annotation { "Feature Type Name" : "Feature", "Feature Type Description" : "" }
export const myFeature = defineFeature(function(context is Context, id is Id, definition is map)
    precondition{}
    {
        {
            var Q0;
            Q0=qCreatedBy(makeId("Top.planeOp"),FACE);
            var sketch = newSketch(context, id + "F0", { "sketchPlane" : qUnion([Q0])});
            skLineSegment(sketch, "E0.bottom", {"start": v(-20, 20) * mm, "end": v(20, 20) * mm});
            skLineSegment(sketch, "E0.top", {"start": v(-20, -20) * mm, "end": v(20, -20) * mm});
            skLineSegment(sketch, "E0.left", {"start": v(-20, 20) * mm, "end": v(-20, -20) * mm});
            skLineSegment(sketch, "E0.right", {"start": v(20, 20) * mm, "end": v(20, -20) * mm});
            skLineSegment(sketch, "E1", {"start": v(-20, 0) * mm, "end": v(20, 0) * mm, "construction": true});
            skSolve(sketch);
        }
        {
            var Q0;
            Q0=makeQuery(id+"F0.imprint","IMPRINT",FACE,{"disambiguationData":[TD([[makeQuery(id+"F0.imprint","IMPRINT",EDGE,{"derivedFrom":sQuery(id+"F0.wireOp",EDGE,"E0.bottom")}),-1.0]])]});
            extrude(context, id + "F1", {"entities" : qUnion([Q0]), "oppositeDirection" : true, "depth" : 40 * mm, "offsetDistance" : 25.4 * mm});
        }
        {
            var Q0;
            Q0=makeQuery(id+"F1.opExtrude","CAP_FACE",FACE,{"disambiguationData":[OSD([sQuery(id+"F0.wireOp",EDGE,"E0.bottom"),sQuery(id+"F0.wireOp",EDGE,"E0.top"),sQuery(id+"F0.wireOp",EDGE,"E0.left"),sQuery(id+"F0.wireOp",EDGE,"E0.right")])],"isStart":true});
            var sketch = newSketch(context, id + "F2", { "sketchPlane" : qUnion([Q0])});
            skLineSegment(sketch, "E2", {"start": v(-3.88, 5.43) * mm, "end": v(-3.88, -20) * mm});
            skLineSegment(sketch, "E3", {"start": v(4.12, 5.43) * mm, "end": v(4.12, -20) * mm});
            skLineSegment(sketch, "E4", {"start": v(4.12, -20) * mm, "end": v(-3.88, -20) * mm});
            skLineSegment(sketch, "E5", {"start": v(-3.88, 5.43) * mm, "end": v(-15, 5.43) * mm});
            skLineSegment(sketch, "E6", {"start": v(-15, 5.43) * mm, "end": v(-15, 12) * mm});
            skLineSegment(sketch, "E7", {"start": v(-15, 12) * mm, "end": v(15, 12) * mm});
            skLineSegment(sketch, "E8", {"start": v(15, 12) * mm, "end": v(15, 5.43) * mm});
            skLineSegment(sketch, "E9", {"start": v(15, 5.43) * mm, "end": v(4.12, 5.43) * mm});
            skSolve(sketch);
        }
        {
            var Q0;
            Q0=makeQuery(id+"F1.opExtrude","SWEPT_FACE",FACE,{"disambiguationData":[OSD([sQuery(id+"F0.wireOp",EDGE,"E0.right")])]});
            var sketch = newSketch(context, id + "F3", { "sketchPlane" : qUnion([Q0])});
            skLineSegment(sketch, "E10", {"start": v(-20, 0) * mm, "end": v(-20, -40) * mm});
            skLineSegment(sketch, "E11", {"start": v(-20, 0) * mm, "end": v(12, 0) * mm});
            skLineSegment(sketch, "E12", {"start": v(-20, -40) * mm, "end": v(12, -40) * mm});
            skLineSegment(sketch, "E13", {"start": v(12, 0) * mm, "end": v(12, -11) * mm});
            skLineSegment(sketch, "E14", {"start": v(12, -11) * mm, "end": v(4, -11) * mm});
            skLineSegment(sketch, "E15", {"start": v(4, -11) * mm, "end": v(4, -8) * mm});
            skLineSegment(sketch, "E16", {"start": v(4, -8) * mm, "end": v(-12, -8) * mm});
            skLineSegment(sketch, "E17", {"start": v(-12, -8) * mm, "end": v(-12, -32) * mm});
            skLineSegment(sketch, "E18", {"start": v(-12, -32) * mm, "end": v(4, -32) * mm});
            skLineSegment(sketch, "E19", {"start": v(4, -32) * mm, "end": v(4, -29) * mm});
            skLineSegment(sketch, "E20", {"start": v(4, -29) * mm, "end": v(12, -29) * mm});
            skLineSegment(sketch, "E21", {"start": v(12, -29) * mm, "end": v(12, -40) * mm});
            skSolve(sketch);
        }
        {
            var Q0;
            Q0=makeQuery(id+"F1.opExtrude","SWEPT_FACE",FACE,{"disambiguationData":[OSD([sQuery(id+"F0.wireOp",EDGE,"E0.top")])]});
            var sketch = newSketch(context, id + "F4", { "sketchPlane" : qUnion([Q0])});
            skLineSegment(sketch, "E22", {"start": v(-4, -7.29) * mm, "end": v(-4, -32) * mm});
            skLineSegment(sketch, "E23", {"start": v(4, -7.29) * mm, "end": v(4, -32) * mm});
            skLineSegment(sketch, "E24", {"start": v(-4, -7.29) * mm, "end": v(-15, -7.29) * mm});
            skLineSegment(sketch, "E25", {"start": v(-15, -7.29) * mm, "end": v(-15, 0) * mm});
            skLineSegment(sketch, "E26", {"start": v(-15, 0) * mm, "end": v(15, 0) * mm});
            skLineSegment(sketch, "E27", {"start": v(15, 0) * mm, "end": v(15, -7.29) * mm});
            skLineSegment(sketch, "E28", {"start": v(15, -7.29) * mm, "end": v(4, -7.29) * mm});
            skLineSegment(sketch, "E29", {"start": v(-4, -32) * mm, "end": v(4, -32) * mm});
            skLineSegment(sketch, "E30.bottom", {"start": v(-15.22, -40) * mm, "end": v(15, -40) * mm});
            skLineSegment(sketch, "E30.top", {"start": v(-15.22, -29) * mm, "end": v(15, -29) * mm});
            skLineSegment(sketch, "E30.left", {"start": v(-15.22, -40) * mm, "end": v(-15.22, -29) * mm});
            skLineSegment(sketch, "E30.right", {"start": v(15, -40) * mm, "end": v(15, -29) * mm});
            skLineSegment(sketch, "E31", {"start": v(-4, -29) * mm, "end": v(-4, -40) * mm});
            skLineSegment(sketch, "E32", {"start": v(4, -32) * mm, "end": v(4, -40) * mm});
            skSolve(sketch);
        }
        {
            var Q0;
            {var subQ2=sQuery(id+"F2.wireOp",EDGE,"E2");Q0=makeQuery(id+"F2.imprint","IMPRINT",FACE,{"disambiguationData":[TD([[makeQuery(id+"F2.imprint","IMPRINT",EDGE,{"derivedFrom":subQ2}),-1.0]])]});}
            extrude(context, id + "F5", {"entities" : qUnion([Q0]), "operationType" : NewBodyOperationType.REMOVE, "oppositeDirection" : true, "depth" : 40 * mm, "offsetDistance" : 25.4 * mm});
        }
        {
            var Q0;
            {var subQ3=sQuery(id+"F3.wireOp",EDGE,"E13");Q0=makeQuery(id+"F3.imprint","IMPRINT",FACE,{"disambiguationData":[TD([[makeQuery(id+"F3.imprint","IMPRINT",EDGE,{"derivedFrom":subQ3}),1.0]])]});}
            extrude(context, id + "F6", {"entities" : qUnion([Q0]), "operationType" : NewBodyOperationType.REMOVE, "oppositeDirection" : true, "depth" : 40 * mm, "offsetDistance" : 25.4 * mm});
        }
        {
            var Q0;
            {var subQ0=sQuery(id+"F4.wireOp",EDGE,"E30.left");Q0=makeQuery(id+"F4.imprint","IMPRINT",FACE,{"disambiguationData":[TD([[makeQuery(id+"F4.imprint","IMPRINT",EDGE,{"derivedFrom":subQ0}),-1.0]])]});}
            var Q1;
            {var subQ0=sQuery(id+"F4.wireOp",EDGE,"E30.right");Q1=makeQuery(id+"F4.imprint","IMPRINT",FACE,{"disambiguationData":[TD([[makeQuery(id+"F4.imprint","IMPRINT",EDGE,{"derivedFrom":subQ0}),1.0]])]});}
            extrude(context, id + "F7", {"entities" : qUnion([Q0, Q1]), "operationType" : NewBodyOperationType.REMOVE, "oppositeDirection" : true, "depth" : 40 * mm, "offsetDistance" : 25.4 * mm});
        }
        {
            var Q0;
            Q0=makeQuery(id+"F7.boolean.opBoolean","COPY",FACE,{"derivedFrom":makeQuery(id+"F7.opExtrude","SWEPT_FACE",FACE,{"disambiguationData":[OSD([sQuery(id+"F4.wireOp",EDGE,"E23"),sQuery(id+"F4.wireOp",EDGE,"E32")])]})});
            var sketch = newSketch(context, id + "F8", { "sketchPlane" : qUnion([Q0])});
            skText(sketch, "E33", { "text": "Cassie Tubbs", "fontName": "OpenSans-Regular.ttf"});
            const initialGuessF8  = {"E33": [-0.016, -0.03785, 1, 0, 0.00283]};
            skSetInitialGuess(sketch, initialGuessF8);
            skSolve(sketch);
        }
        {
            var Q0;
            Q0 = qSketchRegion(id + "F8", true);
            extrude(context, id + "F9", {"entities" : qUnion([Q0]), "operationType" : NewBodyOperationType.REMOVE, "oppositeDirection" : true, "depth" : 5 * mm, "offsetDistance" : 25.4 * mm});
        }
        {
            var Q0;
            Q0=makeQuery(id+"F1.opExtrude","CAP_FACE",FACE,{"disambiguationData":[OSD([sQuery(id+"F0.wireOp",EDGE,"E0.bottom"),sQuery(id+"F0.wireOp",EDGE,"E0.top"),sQuery(id+"F0.wireOp",EDGE,"E0.left"),sQuery(id+"F0.wireOp",EDGE,"E0.right")])],"isStart":false});
            var sketch = newSketch(context, id + "F10", { "sketchPlane" : qUnion([Q0])});
            skLineSegment(sketch, "E34", {"start": v(0.06, 20) * mm, "end": v(0, -12) * mm, "construction": true});
            skCircle(sketch, "E35", {"center": v(0.03, 4) * mm, "radius": 1 * mm});
            skSolve(sketch);
        }
        {
            var Q0;
            Q0 = qSketchRegion(id + "F10", true);
            extrude(context, id + "F11", {"entities" : qUnion([Q0]), "operationType" : NewBodyOperationType.REMOVE, "oppositeDirection" : true, "depth" : 4 * mm, "offsetDistance" : 25.4 * mm});
        }
    });